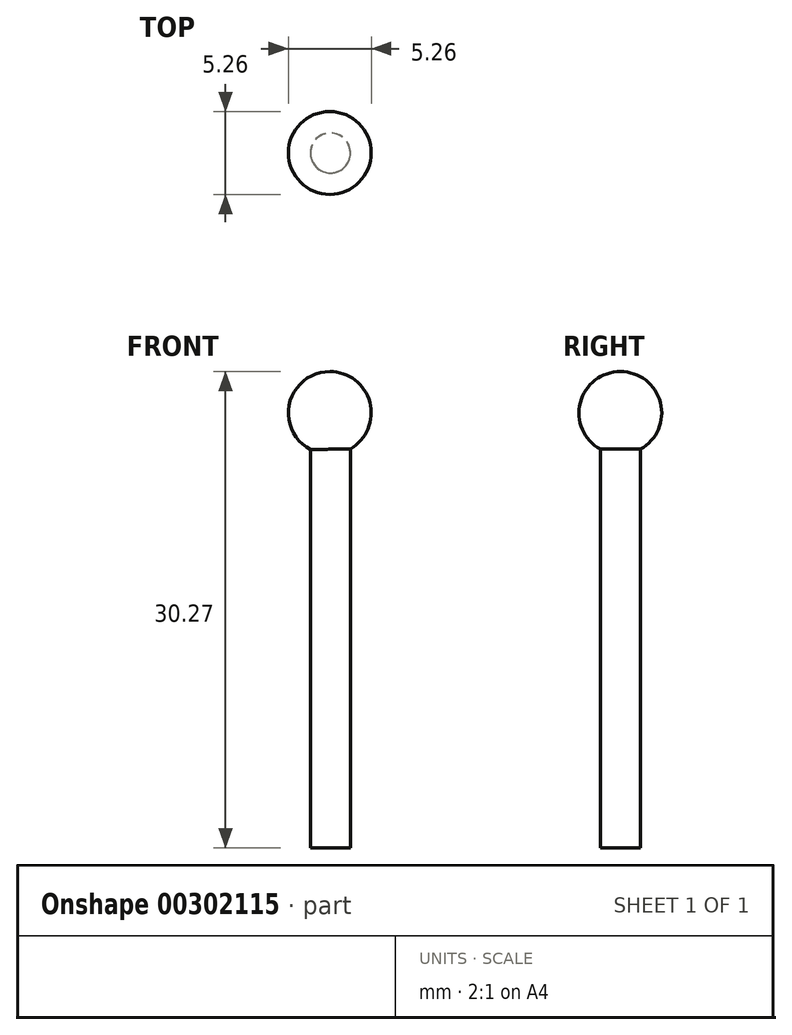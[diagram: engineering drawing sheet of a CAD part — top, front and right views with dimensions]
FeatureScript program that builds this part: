
annotation { "Feature Type Name" : "Feature", "Feature Type Description" : "" }
export const myFeature = defineFeature(function(context is Context, id is Id, definition is map)
    precondition{}
    {
        {
            var Q0;
            Q0=qCreatedBy(makeId("Front.planeOp"),FACE);
            var sketch = newSketch(context, id + "F0", { "sketchPlane" : qUnion([Q0])});
            skLineSegment(sketch, "E0", {"start": v(-3.06, 25.4) * mm, "end": v(-3.06, 0) * mm});
            skLineSegment(sketch, "E1", {"start": v(-3.06, 0) * mm, "end": v(-4.33, 0) * mm});
            skLineSegment(sketch, "E2", {"start": v(-4.33, 0) * mm, "end": v(-4.33, 25.4) * mm});
            skLineSegment(sketch, "E3", {"start": v(-4.33, 25.4) * mm, "end": v(-3.06, 25.4) * mm});
            skSolve(sketch);
        }
        {
            var Q0;
            Q0 = qSketchRegion(id + "F0", true);
            var Q1;
            Q1=sQuery(id+"F0.wireOp",EDGE,"E0");
            revolve(context, id + "F1", {"entities" : qUnion([Q0]), "axis" : qUnion([Q1]), "revolveType" : RevolveType.FULL});
        }
        {
            var Q0;
            Q0=qCreatedBy(makeId("Front.planeOp"),FACE);
            var sketch = newSketch(context, id + "F2", { "sketchPlane" : qUnion([Q0])});
            skArc(sketch, "E4", {"start": v(-3.1, 30.27) * mm, "mid": v(-5.73, 27.64) * mm, "end": v(-3.1, 25) * mm});
            skLineSegment(sketch, "E5", {"start": v(-3.1, 25) * mm, "end": v(-3.1, 30.27) * mm});
            skSolve(sketch);
        }
        {
            var Q0;
            Q0 = qSketchRegion(id + "F2", true);
            var Q1;
            Q1=sQuery(id+"F2.wireOp",EDGE,"E5");
            revolve(context, id + "F3", {"operationType" : NewBodyOperationType.ADD, "entities" : qUnion([Q0]), "axis" : qUnion([Q1]), "revolveType" : RevolveType.FULL});
        }
    });
